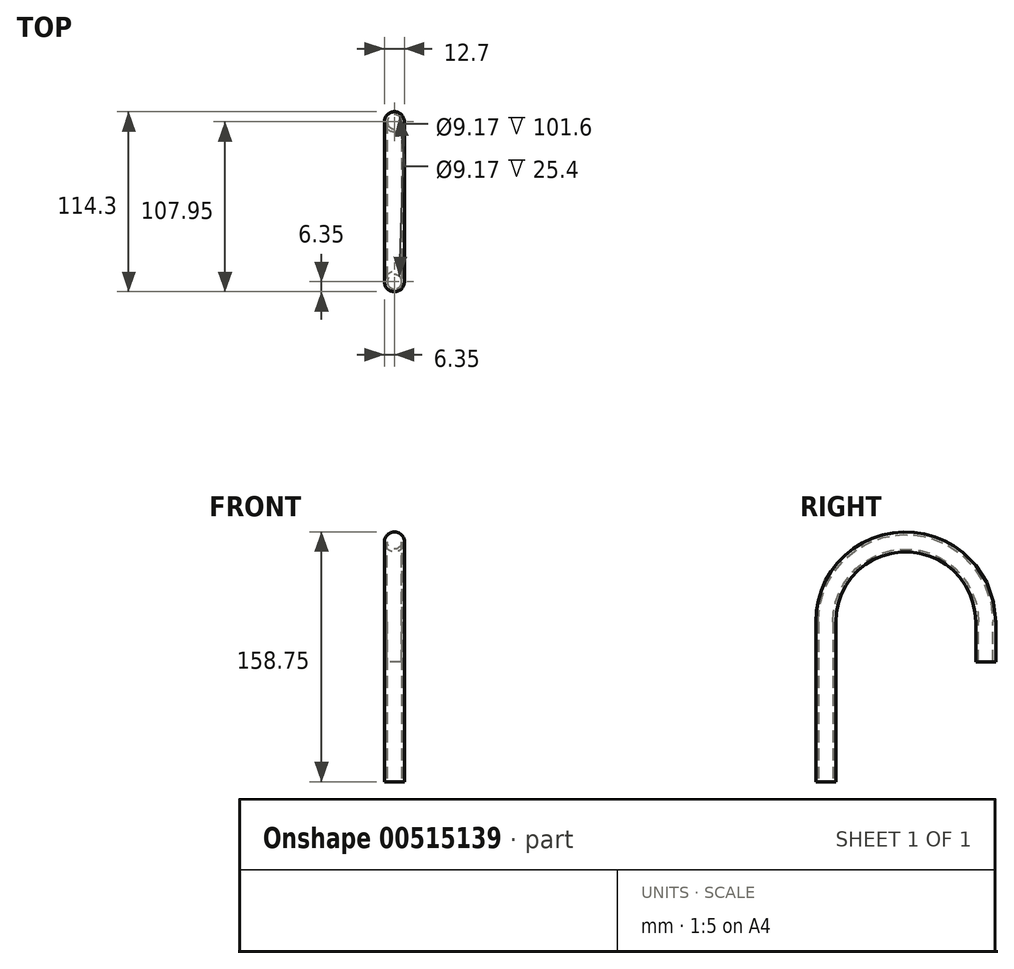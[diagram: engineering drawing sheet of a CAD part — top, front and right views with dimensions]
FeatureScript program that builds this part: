
annotation { "Feature Type Name" : "Feature", "Feature Type Description" : "" }
export const myFeature = defineFeature(function(context is Context, id is Id, definition is map)
    precondition{}
    {
        {
            var Q0;
            Q0=qCreatedBy(makeId("Right.planeOp"),FACE);
            var sketch = newSketch(context, id + "F0", { "sketchPlane" : qUnion([Q0])});
            skLineSegment(sketch, "E0", {"start": v(0, 0) * mm, "end": v(0, 25.4) * mm});
            skArc(sketch, "E1", {"start": v(0, 25.4) * mm, "mid": v(-50.8, 76.2) * mm, "end": v(-101.6, 25.4) * mm});
            skLineSegment(sketch, "E2", {"start": v(-101.6, 25.4) * mm, "end": v(-101.6, -76.2) * mm});
            skSolve(sketch);
        }
        {
            var Q0;
            Q0=qCreatedBy(makeId("Top.planeOp"),FACE);
            var sketch = newSketch(context, id + "F1", { "sketchPlane" : qUnion([Q0])});
            skCircle(sketch, "E3", {"center": v(0, 0) * mm, "radius": 6.35 * mm});
            skCircle(sketch, "E4", {"center": v(0, 0) * mm, "radius": 4.59 * mm});
            skSolve(sketch);
        }
        {
            var Q0;
            Q0=makeQuery(id+"F1.imprint","IMPRINT",FACE,{"disambiguationData":[TD([[makeQuery(id+"F1.imprint","IMPRINT",EDGE,{"derivedFrom":sQuery(id+"F1.wireOp",EDGE,"E3")}),1.0]])]});
            var Q1;
            Q1=sQuery(id+"F0.wireOp",EDGE,"E0");
            var Q2;
            Q2=sQuery(id+"F0.wireOp",EDGE,"E1");
            var Q3;
            Q3=sQuery(id+"F0.wireOp",EDGE,"E2");
            sweep(context, id + "F2", {"profiles" : qUnion([Q0]), "path" : qUnion([Q1, Q2, Q3])});
        }
    });
